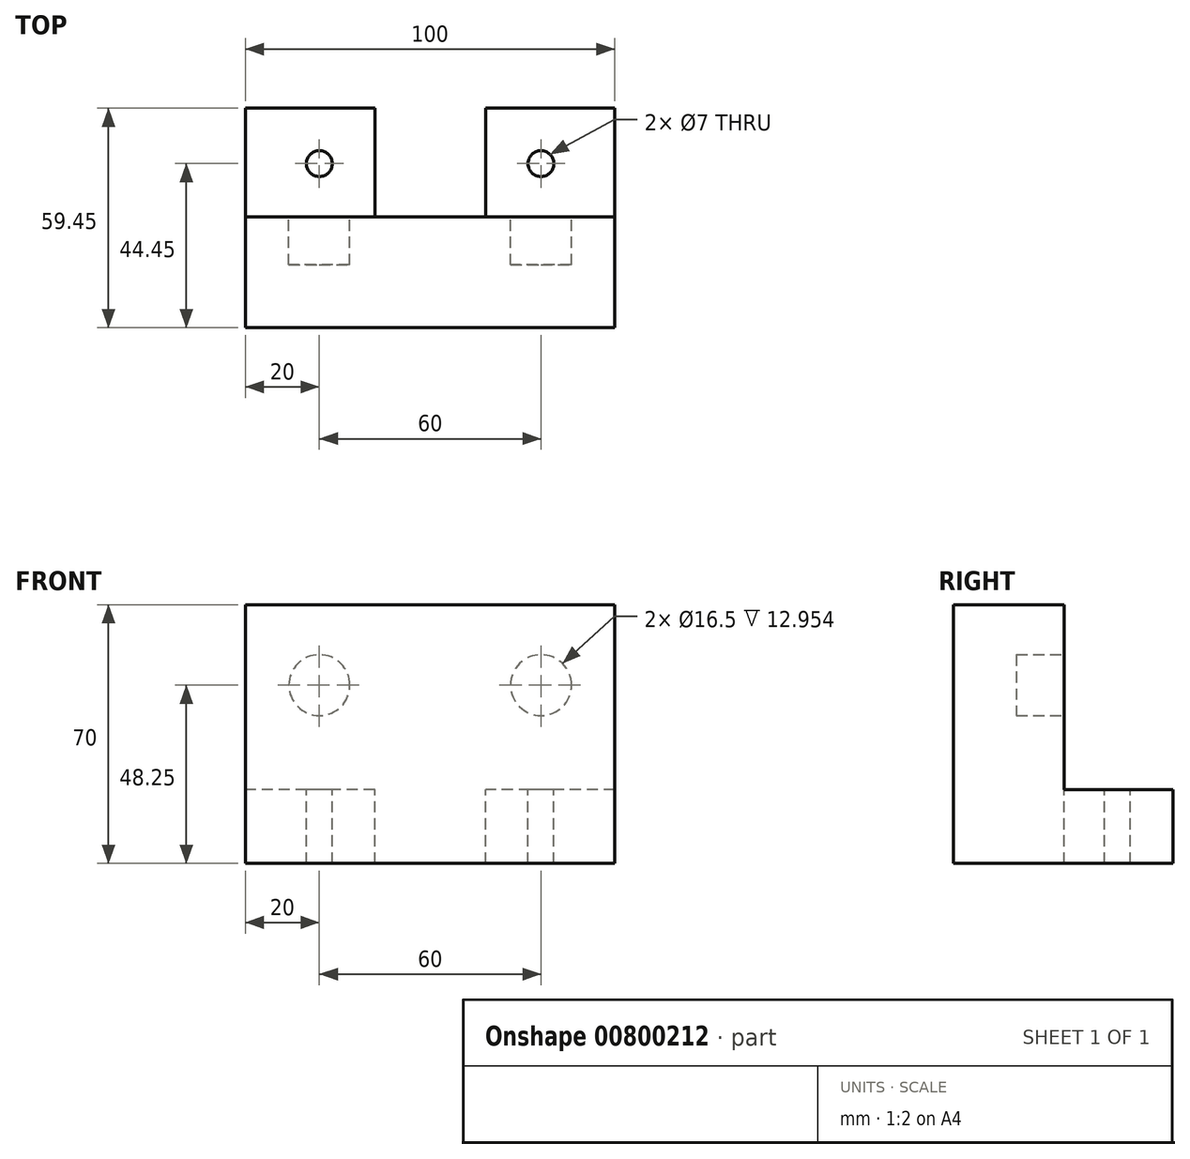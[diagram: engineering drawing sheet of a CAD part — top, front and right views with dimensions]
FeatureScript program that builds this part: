
annotation { "Feature Type Name" : "Feature", "Feature Type Description" : "" }
export const myFeature = defineFeature(function(context is Context, id is Id, definition is map)
    precondition{}
    {
        {
            var Q0;
            Q0=qCreatedBy(makeId("Right.planeOp"),FACE);
            var sketch = newSketch(context, id + "F0", { "sketchPlane" : qUnion([Q0])});
            skLineSegment(sketch, "E0", {"start": v(59.45, 0) * mm, "end": v(0, 0) * mm});
            skLineSegment(sketch, "E1", {"start": v(0, 0) * mm, "end": v(0, 70) * mm});
            skLineSegment(sketch, "E2", {"start": v(0, 70) * mm, "end": v(30, 70) * mm});
            skLineSegment(sketch, "E3", {"start": v(30, 70) * mm, "end": v(30, 20) * mm});
            skLineSegment(sketch, "E4", {"start": v(30, 20) * mm, "end": v(59.45, 20) * mm});
            skLineSegment(sketch, "E5", {"start": v(59.45, 20) * mm, "end": v(59.45, 0) * mm});
            skSolve(sketch);
        }
        {
            var Q0;
            Q0 = qSketchRegion(id + "F0", true);
            extrude(context, id + "F1", {"entities" : qUnion([Q0]), "depth" : 100 * mm, "offsetDistance" : 25.4 * mm});
        }
        {
            var Q0;
            Q0=makeQuery(id+"F1.opExtrude","SWEPT_FACE",FACE,{"disambiguationData":[OSD([sQuery(id+"F0.wireOp",EDGE,"E3")])]});
            var sketch = newSketch(context, id + "F2", { "sketchPlane" : qUnion([Q0])});
            skCircle(sketch, "E6", {"center": v(-80, 48.25) * mm, "radius": 8.25 * mm});
            skCircle(sketch, "E7", {"center": v(-20, 48.25) * mm, "radius": 8.25 * mm});
            skSolve(sketch);
        }
        {
            var Q0;
            Q0 = qSketchRegion(id + "F2", true);
            extrude(context, id + "F3", {"entities" : qUnion([Q0]), "operationType" : NewBodyOperationType.REMOVE, "oppositeDirection" : true, "depth" : 12.95 * mm, "offsetDistance" : 25.4 * mm});
        }
        {
            var Q0;
            Q0=makeQuery(id+"F1.opExtrude","SWEPT_FACE",FACE,{"disambiguationData":[OSD([sQuery(id+"F0.wireOp",EDGE,"E4")])]});
            var sketch = newSketch(context, id + "F4", { "sketchPlane" : qUnion([Q0])});
            skCircle(sketch, "E8", {"center": v(80, 44.45) * mm, "radius": 3.5 * mm});
            skCircle(sketch, "E9", {"center": v(20, 44.45) * mm, "radius": 3.5 * mm});
            skSolve(sketch);
        }
        {
            var Q0;
            Q0 = qSketchRegion(id + "F4", true);
            extrude(context, id + "F5", {"entities" : qUnion([Q0]), "operationType" : NewBodyOperationType.REMOVE, "endBound" : BoundingType.UP_TO_NEXT, "oppositeDirection" : true, "depth" : 25.4 * mm, "offsetDistance" : 25.4 * mm});
        }
        {
            var Q0;
            Q0=makeQuery(id+"F1.opExtrude","SWEPT_FACE",FACE,{"disambiguationData":[OSD([sQuery(id+"F0.wireOp",EDGE,"E4")])]});
            var sketch = newSketch(context, id + "F6", { "sketchPlane" : qUnion([Q0])});
            skLineSegment(sketch, "E10.bottom", {"start": v(35, 59.45) * mm, "end": v(65, 59.45) * mm});
            skLineSegment(sketch, "E10.top", {"start": v(35, 30) * mm, "end": v(65, 30) * mm});
            skLineSegment(sketch, "E10.left", {"start": v(35, 59.45) * mm, "end": v(35, 30) * mm});
            skLineSegment(sketch, "E10.right", {"start": v(65, 59.45) * mm, "end": v(65, 30) * mm});
            skSolve(sketch);
        }
        {
            var Q0;
            Q0 = qSketchRegion(id + "F6", true);
            extrude(context, id + "F7", {"entities" : qUnion([Q0]), "operationType" : NewBodyOperationType.REMOVE, "endBound" : BoundingType.UP_TO_NEXT, "oppositeDirection" : true, "depth" : 25.4 * mm, "offsetDistance" : 25.4 * mm});
        }
    });
